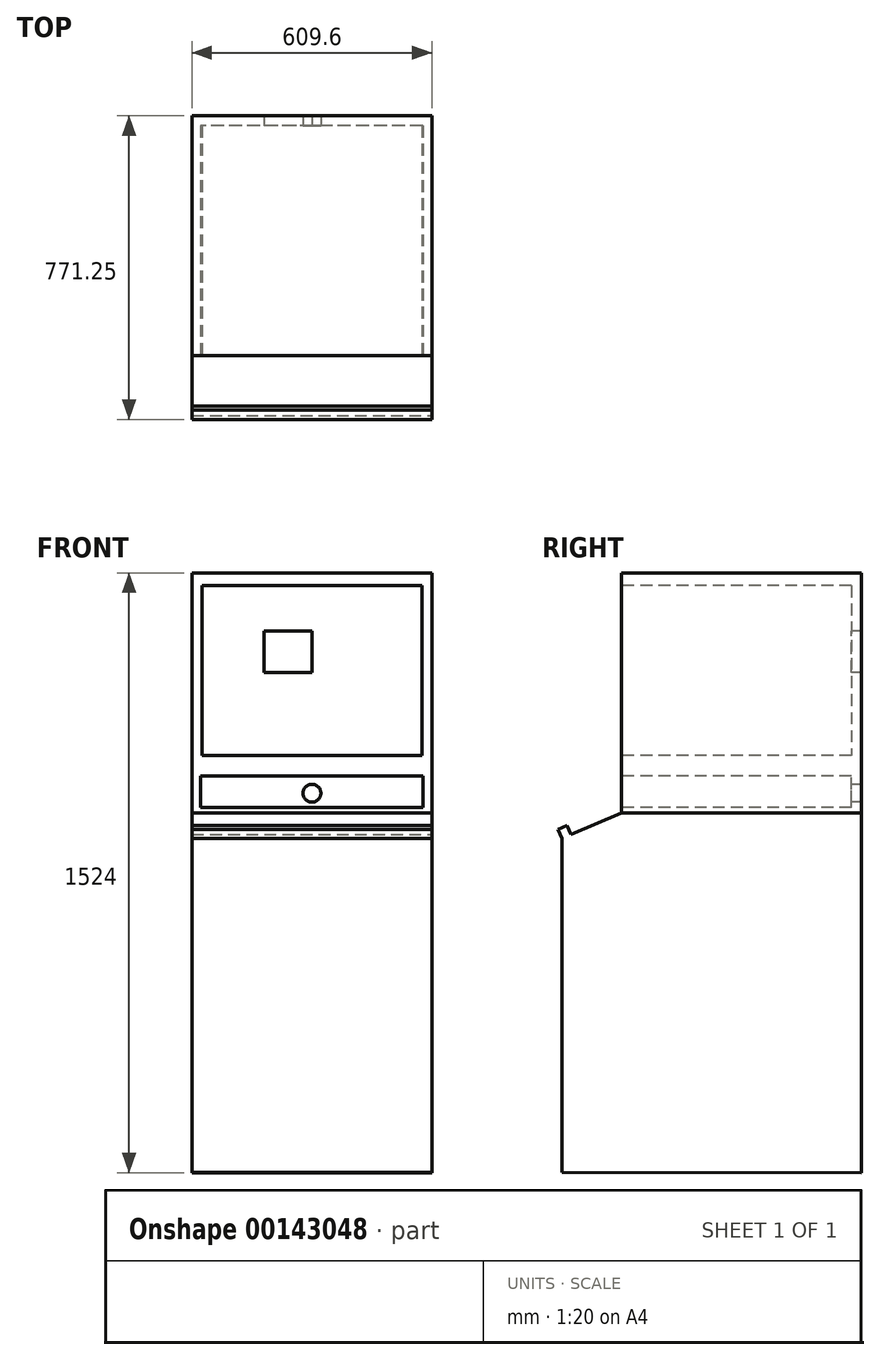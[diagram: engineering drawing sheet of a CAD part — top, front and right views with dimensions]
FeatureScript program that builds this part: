
annotation { "Feature Type Name" : "Feature", "Feature Type Description" : "" }
export const myFeature = defineFeature(function(context is Context, id is Id, definition is map)
    precondition{}
    {
        {
            var Q0;
            Q0=qCreatedBy(makeId("Top.planeOp"),FACE);
            var sketch = newSketch(context, id + "F0", { "sketchPlane" : qUnion([Q0])});
            skLineSegment(sketch, "E0.bottom", {"start": v(304.8, 304.8) * mm, "end": v(-304.8, 304.8) * mm});
            skLineSegment(sketch, "E0.top", {"start": v(304.8, -304.8) * mm, "end": v(-304.8, -304.8) * mm});
            skLineSegment(sketch, "E0.left", {"start": v(304.8, 304.8) * mm, "end": v(304.8, -304.8) * mm});
            skLineSegment(sketch, "E0.right", {"start": v(-304.8, 304.8) * mm, "end": v(-304.8, -304.8) * mm});
            skPoint(sketch, "E0.middle", {"position": v(0, 0) * mm});
            skSolve(sketch);
        }
        {
            var Q0;
            Q0 = qSketchRegion(id + "F0", true);
            extrude(context, id + "F1", {"entities" : qUnion([Q0]), "depth" : 609.6 * mm});
        }
        {
            var Q0;
            Q0=makeQuery(id+"F1.opExtrude","SWEPT_FACE",FACE,{"disambiguationData":[OSD([sQuery(id+"F0.wireOp",EDGE,"E0.top")])]});
            var sketch = newSketch(context, id + "F2", { "sketchPlane" : qUnion([Q0])});
            skLineSegment(sketch, "E1.bottom", {"start": v(279.4, 577.43) * mm, "end": v(-279.4, 577.43) * mm});
            skLineSegment(sketch, "E1.top", {"start": v(279.4, 145.63) * mm, "end": v(-279.4, 145.63) * mm});
            skLineSegment(sketch, "E1.left", {"start": v(279.4, 577.43) * mm, "end": v(279.4, 145.63) * mm});
            skLineSegment(sketch, "E1.right", {"start": v(-279.4, 577.43) * mm, "end": v(-279.4, 145.63) * mm});
            skPoint(sketch, "E1.middle", {"position": v(0, 361.53) * mm});
            skPoint(sketch, "E1.middle.positionSnap0", {"position": v(0, 609.6) * mm});
            skPoint(sketch, "E1.centerSnap0", {"position": v(0, 609.6) * mm});
            skLineSegment(sketch, "E2.bottom", {"start": v(282.45, 13.64) * mm, "end": v(-282.45, 13.64) * mm});
            skLineSegment(sketch, "E2.top", {"start": v(282.45, 94.13) * mm, "end": v(-282.45, 94.13) * mm});
            skLineSegment(sketch, "E2.left", {"start": v(282.45, 13.64) * mm, "end": v(282.45, 94.13) * mm});
            skLineSegment(sketch, "E2.right", {"start": v(-282.45, 13.64) * mm, "end": v(-282.45, 94.13) * mm});
            skPoint(sketch, "E2.middle", {"position": v(0, 53.88) * mm});
            skPoint(sketch, "E2.middle.positionSnap0", {"position": v(0, 0) * mm});
            skPoint(sketch, "E2.centerSnap0", {"position": v(0, 0) * mm});
            skSolve(sketch);
        }
        {
            var Q0;
            Q0 = qSketchRegion(id + "F2", true);
            extrude(context, id + "F3", {"entities" : qUnion([Q0]), "operationType" : NewBodyOperationType.REMOVE, "oppositeDirection" : true, "depth" : 584.2 * mm});
        }
        {
            var Q0;
            Q0=makeQuery(id+"F3.boolean.opBoolean","COPY",FACE,{"derivedFrom":makeQuery(id+"F3.opExtrude","CAP_FACE",FACE,{"disambiguationData":[OSD([sQuery(id+"F2.wireOp",EDGE,"E1.bottom"),sQuery(id+"F2.wireOp",EDGE,"E1.top"),sQuery(id+"F2.wireOp",EDGE,"E1.left"),sQuery(id+"F2.wireOp",EDGE,"E1.right")])],"isStart":false})});
            var sketch = newSketch(context, id + "F4", { "sketchPlane" : qUnion([Q0])});
            skPoint(sketch, "E3.firstSnap0", {"position": v(0, 145.63) * mm});
            skLineSegment(sketch, "E3.bottom", {"start": v(0, 356.87) * mm, "end": v(-121.88, 356.87) * mm});
            skLineSegment(sketch, "E3.top", {"start": v(0, 461.34) * mm, "end": v(-121.88, 461.34) * mm});
            skLineSegment(sketch, "E3.left", {"start": v(0, 356.87) * mm, "end": v(0, 461.34) * mm});
            skLineSegment(sketch, "E3.right", {"start": v(-121.88, 356.87) * mm, "end": v(-121.88, 461.34) * mm});
            skCircle(sketch, "E4", {"center": v(0, 49.68) * mm, "radius": 22.7 * mm});
            skSolve(sketch);
        }
        {
            var Q0;
            Q0=makeQuery(id+"F4.imprint","IMPRINT",FACE,{"disambiguationData":[TD([[makeQuery(id+"F4.imprint","IMPRINT",EDGE,{"derivedFrom":sQuery(id+"F4.wireOp",EDGE,"E3.bottom")}),-1.0]])]});
            extrude(context, id + "F5", {"entities" : qUnion([Q0]), "operationType" : NewBodyOperationType.REMOVE, "oppositeDirection" : true, "depth" : 25.4 * mm});
        }
        {
            var Q0;
            Q0 = qSketchRegion(id + "F4", true);
            extrude(context, id + "F6", {"entities" : qUnion([Q0]), "operationType" : NewBodyOperationType.REMOVE, "oppositeDirection" : true, "depth" : 25.4 * mm});
        }
        {
            var Q0;
            Q0=makeQuery(id+"F1.opExtrude","SWEPT_FACE",FACE,{"disambiguationData":[OSD([sQuery(id+"F0.wireOp",EDGE,"E0.left")])]});
            var sketch = newSketch(context, id + "F7", { "sketchPlane" : qUnion([Q0])});
            skLineSegment(sketch, "E5", {"start": v(-304.8, 0) * mm, "end": v(-456.38, -65.44) * mm});
            skLineSegment(sketch, "E6", {"start": v(304.8, 0) * mm, "end": v(304.8, -914.4) * mm});
            skLineSegment(sketch, "E7", {"start": v(-456.38, -65.44) * mm, "end": v(-456.38, -913.8) * mm});
            skLineSegment(sketch, "E8", {"start": v(304.8, -914.4) * mm, "end": v(-456.38, -913.8) * mm});
            skSolve(sketch);
        }
        {
            var Q0;
            Q0 = qSketchRegion(id + "F7", true);
            var Q1;
            Q1=makeQuery(id+"F7.imprint","IMPRINT",FACE,{"disambiguationData":[TD([[makeQuery(id+"F7.imprint","IMPRINT",EDGE,{"derivedFrom":sQuery(id+"F7.wireOp",EDGE,"E5")}),1.0]])]});
            extrude(context, id + "F8", {"entities" : qUnion([Q0, Q1]), "oppositeDirection" : true, "depth" : 609.6 * mm});
        }
        {
            var Q0;
            Q0=makeQuery(id+"F8.opExtrude","SWEPT_FACE",FACE,{"disambiguationData":[OSD([sQuery(id+"F7.wireOp",EDGE,"E5")])]});
            var sketch = newSketch(context, id + "F9", { "sketchPlane" : qUnion([Q0])});
            skLineSegment(sketch, "E9.bottom", {"start": v(-304.8, -419.54) * mm, "end": v(304.8, -419.54) * mm});
            skLineSegment(sketch, "E9.top", {"start": v(-304.8, -444.94) * mm, "end": v(304.8, -444.94) * mm});
            skLineSegment(sketch, "E9.left", {"start": v(-304.8, -419.54) * mm, "end": v(-304.8, -444.94) * mm});
            skLineSegment(sketch, "E9.right", {"start": v(304.8, -419.54) * mm, "end": v(304.8, -444.94) * mm});
            skSolve(sketch);
        }
        {
            var Q0;
            Q0 = qSketchRegion(id + "F9", true);
            extrude(context, id + "F10", {"entities" : qUnion([Q0]), "operationType" : NewBodyOperationType.ADD, "depth" : 25.4 * mm});
        }
    });
